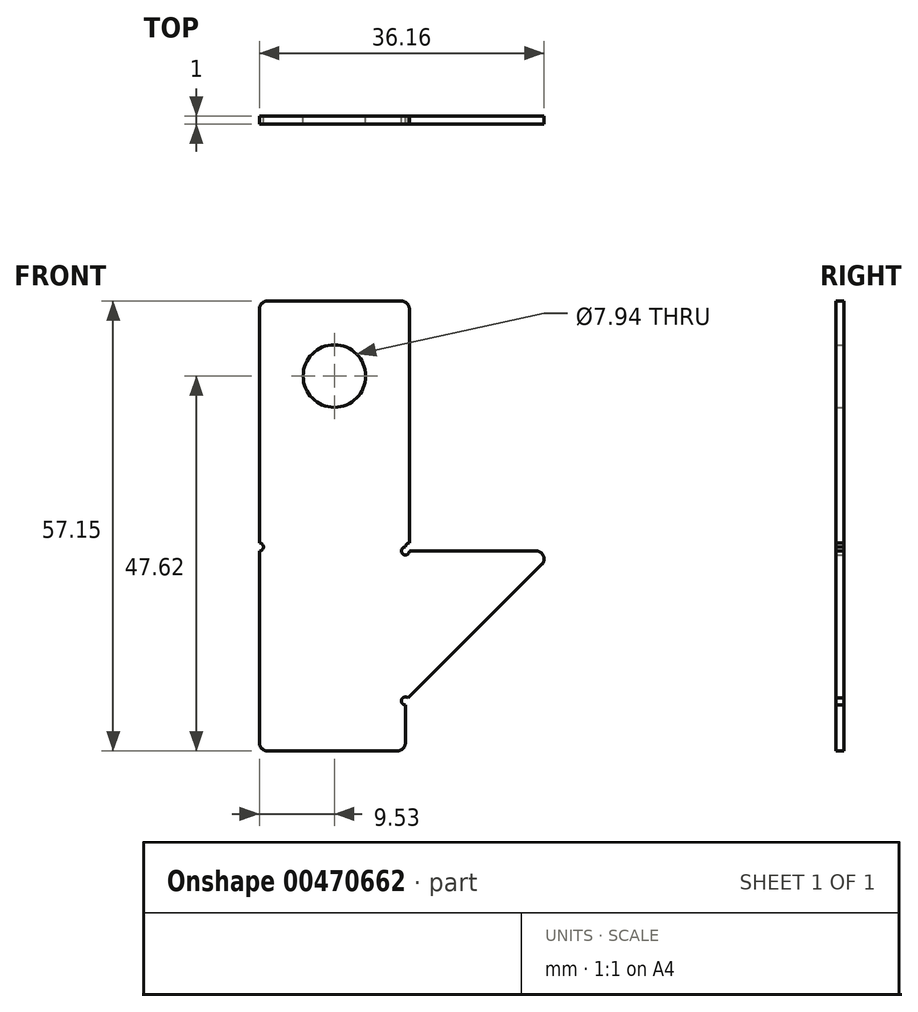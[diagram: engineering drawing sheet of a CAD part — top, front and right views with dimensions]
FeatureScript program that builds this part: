
annotation { "Feature Type Name" : "Feature", "Feature Type Description" : "" }
export const myFeature = defineFeature(function(context is Context, id is Id, definition is map)
    precondition{}
    {
        {
            var Q0;
            Q0=qCreatedBy(makeId("Front.planeOp"),FACE);
            var sketch = newSketch(context, id + "F0", { "sketchPlane" : qUnion([Q0])});
            skCircle(sketch, "E0.cCircle", {"center": v(0, 0) * mm, "radius": 6.35 * mm, "construction": true});
            skCircle(sketch, "E1", {"center": v(0, 0) * mm, "radius": 3.97 * mm});
            skLineSegment(sketch, "E2", {"start": v(0, 9.53) * mm, "end": v(-8.5, 9.53) * mm});
            skLineSegment(sketch, "E3", {"start": v(-9.53, 8.5) * mm, "end": v(-9.52, -21.2) * mm});
            skPoint(sketch, "E4.visualSharp", {"position": v(-9.53, 9.53) * mm});
            skArc(sketch, "E4.filletArc", {"start": v(-8.5, 9.53) * mm, "mid": v(-9.23, 9.23) * mm, "end": v(-9.53, 8.5) * mm});
            skLineSegment(sketch, "E5", {"start": v(-9.52, -22.23) * mm, "end": v(9.02, -22.23) * mm, "construction": true});
            skLineSegment(sketch, "E6.0", {"start": v(-7.33, 0) * mm, "end": v(-3.67, 6.35) * mm, "construction": true});
            skLineSegment(sketch, "E6.1", {"start": v(-3.67, 6.35) * mm, "end": v(3.67, 6.35) * mm, "construction": true});
            skLineSegment(sketch, "E6.2", {"start": v(3.67, 6.35) * mm, "end": v(7.33, 0) * mm, "construction": true});
            skLineSegment(sketch, "E6.3", {"start": v(7.33, 0) * mm, "end": v(3.67, -6.35) * mm, "construction": true});
            skLineSegment(sketch, "E6.4", {"start": v(3.67, -6.35) * mm, "end": v(-3.67, -6.35) * mm, "construction": true});
            skLineSegment(sketch, "E6.5", {"start": v(-3.67, -6.35) * mm, "end": v(-7.33, 0) * mm, "construction": true});
            skPoint(sketch, "E6.0.midPoint", {"position": v(-5.5, 3.18) * mm});
            skLineSegment(sketch, "E7", {"start": v(-9.52, -22.23) * mm, "end": v(-9.52, -46.6) * mm});
            skLineSegment(sketch, "E8", {"start": v(-8.5, -47.62) * mm, "end": v(0, -47.62) * mm});
            skPoint(sketch, "E9.visualSharp", {"position": v(-9.52, -47.62) * mm});
            skArc(sketch, "E9.filletArc", {"start": v(-9.52, -46.6) * mm, "mid": v(-9.23, -47.33) * mm, "end": v(-8.5, -47.62) * mm});
            skArc(sketch, "E10", {"start": v(-9.52, -22.23) * mm, "mid": v(-9.02, -21.72) * mm, "end": v(-9.52, -21.2) * mm});
            skLineSegment(sketch, "E11.MirrorCS", {"start": v(0, 9.53) * mm, "end": v(8.5, 9.53) * mm});
            skArc(sketch, "E12.MirrorCS", {"start": v(8.5, 9.53) * mm, "mid": v(9.23, 9.23) * mm, "end": v(9.53, 8.5) * mm});
            skLineSegment(sketch, "E13.MirrorCS", {"start": v(9.53, 8.5) * mm, "end": v(9.52, -21.2) * mm});
            skLineSegment(sketch, "E14", {"start": v(0, -47.62) * mm, "end": v(8, -47.62) * mm});
            skLineSegment(sketch, "E15", {"start": v(9.02, -46.6) * mm, "end": v(9.02, -41.78) * mm});
            skLineSegment(sketch, "E16", {"start": v(9.38, -40.92) * mm, "end": v(26.33, -23.96) * mm});
            skArc(sketch, "E17", {"start": v(9.38, -40.92) * mm, "mid": v(8.55, -41.08) * mm, "end": v(9.02, -41.78) * mm});
            skPoint(sketch, "E18.visualSharp", {"position": v(9.02, -47.62) * mm});
            skArc(sketch, "E18.filletArc", {"start": v(8, -47.62) * mm, "mid": v(8.72, -47.33) * mm, "end": v(9.02, -46.6) * mm});
            skLineSegment(sketch, "E19", {"start": v(-9.52, -21.72) * mm, "end": v(9.52, -21.72) * mm, "construction": true});
            skPoint(sketch, "E19.endSnap0", {"position": v(-9.02, -21.72) * mm});
            skPoint(sketch, "E20.orphan", {"position": v(0, -22.23) * mm});
            skLineSegment(sketch, "E21", {"start": v(9.02, -22.23) * mm, "end": v(9.02, -41.28) * mm, "construction": true});
            skLineSegment(sketch, "E22", {"start": v(25.61, -22.23) * mm, "end": v(9.53, -22.23) * mm});
            skPoint(sketch, "E23.visualSharp", {"position": v(28.07, -22.23) * mm});
            skArc(sketch, "E23.filletArc", {"start": v(26.33, -23.96) * mm, "mid": v(26.55, -22.85) * mm, "end": v(25.61, -22.23) * mm});
            skPoint(sketch, "E24.orphan", {"position": v(0, -21.72) * mm});
            skArc(sketch, "E25", {"start": v(9.52, -21.2) * mm, "mid": v(9.17, -21.36) * mm, "end": v(9.02, -21.72) * mm});
            skArc(sketch, "E26", {"start": v(9.02, -21.72) * mm, "mid": v(8.66, -22.58) * mm, "end": v(9.53, -22.23) * mm});
            skSolve(sketch);
        }
        {
            var Q0;
            Q0=makeQuery(id+"F0.imprint","IMPRINT",FACE,{"disambiguationData":[TD([[makeQuery(id+"F0.imprint","IMPRINT",EDGE,{"derivedFrom":sQuery(id+"F0.wireOp",EDGE,"E1")}),-1.0]])]});
            extrude(context, id + "F1", {"entities" : qUnion([Q0]), "depth" : 1 * mm, "offsetDistance" : 25.4 * mm});
        }
    });
